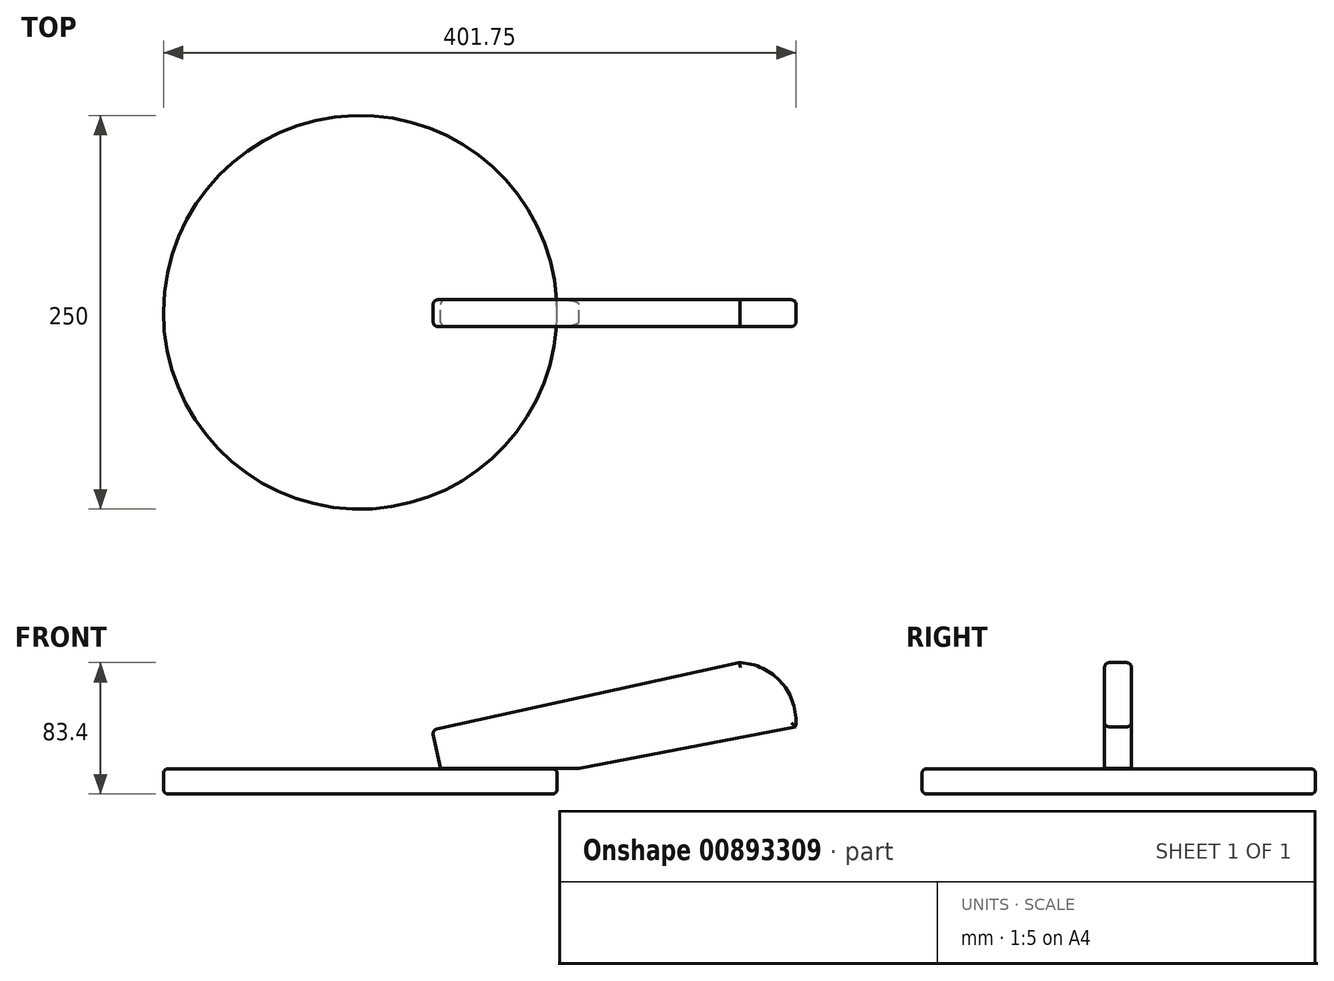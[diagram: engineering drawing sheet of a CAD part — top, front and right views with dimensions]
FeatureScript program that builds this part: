
annotation { "Feature Type Name" : "Feature", "Feature Type Description" : "" }
export const myFeature = defineFeature(function(context is Context, id is Id, definition is map)
    precondition{}
    {
        {
            var Q0;
            Q0=qCreatedBy(makeId("Top.planeOp"),FACE);
            var sketch = newSketch(context, id + "F0", { "sketchPlane" : qUnion([Q0])});
            skCircle(sketch, "E0", {"center": v(0, 0) * mm, "radius": 125 * mm});
            skSolve(sketch);
        }
        {
            var Q0;
            Q0 = qSketchRegion(id + "F0", true);
            extrude(context, id + "F1", {"entities" : qUnion([Q0]), "depth" : 16 * mm, "offsetDistance" : 25 * mm});
        }
        {
            var Q0;
            Q0=qCreatedBy(makeId("Front.planeOp"),FACE);
            var sketch = newSketch(context, id + "F2", { "sketchPlane" : qUnion([Q0])});
            skLineSegment(sketch, "E1", {"start": v(-19, 40.24) * mm, "end": v(69, 40.24) * mm});
            skLineSegment(sketch, "E2", {"start": v(69, 40.24) * mm, "end": v(206.48, 66.66) * mm});
            skLineSegment(sketch, "E3", {"start": v(-19, 40.24) * mm, "end": v(-24.35, 64.66) * mm});
            skLineSegment(sketch, "E4", {"start": v(-24.35, 64.66) * mm, "end": v(171.03, 107.4) * mm});
            skArc(sketch, "E5", {"start": v(206.48, 66.66) * mm, "mid": v(197.5, 94.64) * mm, "end": v(171.03, 107.4) * mm});
            skSolve(sketch);
        }
        {
            var Q0;
            Q0=makeQuery(id+"F2.imprint","IMPRINT",FACE,{"disambiguationData":[TD([[makeQuery(id+"F2.imprint","IMPRINT",EDGE,{"derivedFrom":sQuery(id+"F2.wireOp",EDGE,"E1")}),1.0]])]});
            extrude(context, id + "F3", {"entities" : qUnion([Q0]), "depth" : 17 * mm, "offsetDistance" : 25 * mm});
        }
        {
            var Q0;
            Q0=makeQuery(id+"F1.opExtrude","CAP_EDGE",EDGE,{"disambiguationData":[OSD([sQuery(id+"F0.wireOp",EDGE,"E0")])],"isStart":false});
            var Q1;
            Q1=makeQuery(id+"F1.opExtrude","CAP_EDGE",EDGE,{"disambiguationData":[OSD([sQuery(id+"F0.wireOp",EDGE,"E0")])],"isStart":true});
            var Q2;
            Q2=makeQuery(id+"F3.opExtrude","CAP_EDGE",EDGE,{"disambiguationData":[OSD([sQuery(id+"F2.wireOp",EDGE,"E4")])],"isStart":false});
            var Q3;
            Q3=makeQuery(id+"F3.opExtrude","CAP_EDGE",EDGE,{"disambiguationData":[OSD([sQuery(id+"F2.wireOp",EDGE,"E5")])],"isStart":false});
            var Q4;
            Q4=makeQuery(id+"F3.opExtrude","CAP_EDGE",EDGE,{"disambiguationData":[OSD([sQuery(id+"F2.wireOp",EDGE,"E5")])],"isStart":true});
            var Q5;
            Q5=makeQuery(id+"F3.opExtrude","CAP_EDGE",EDGE,{"disambiguationData":[OSD([sQuery(id+"F2.wireOp",EDGE,"E4")])],"isStart":true});
            var Q6;
            Q6=makeQuery(id+"F3.opExtrude","CAP_EDGE",EDGE,{"disambiguationData":[OSD([sQuery(id+"F2.wireOp",EDGE,"E2")])],"isStart":true});
            var Q7;
            Q7=makeQuery(id+"F3.opExtrude","CAP_EDGE",EDGE,{"disambiguationData":[OSD([sQuery(id+"F2.wireOp",EDGE,"E2")])],"isStart":false});
            var Q8;
            Q8=makeQuery(id+"F3.opExtrude","CAP_EDGE",EDGE,{"disambiguationData":[OSD([sQuery(id+"F2.wireOp",EDGE,"E3")])],"isStart":false});
            var Q9;
            Q9=makeQuery(id+"F3.opExtrude","CAP_EDGE",EDGE,{"disambiguationData":[OSD([sQuery(id+"F2.wireOp",EDGE,"E3")])],"isStart":true});
            var Q10;
            Q10=makeQuery(id+"F3.opExtrude","SWEPT_EDGE",EDGE,{"disambiguationData":[OSD([sQuery(id+"F2.wireOp",EDGE,"E3"),sQuery(id+"F2.wireOp",EDGE,"E4")])]});
            fillet(context, id + "F4", {"entities" : qUnion([Q0, Q1, Q2, Q3, Q4, Q5, Q6, Q7, Q8, Q9, Q10]), "radius" : 3 * mm, "tangentPropagation" : true, "allowEdgeOverflow" : false});
        }
        {
            var Q0;
            Q0=makeQuery(id+"F3.opExtrude","SWEPT_BODY",BODY,{"disambiguationData":[OSD([sQuery(id+"F2.wireOp",EDGE,"E1"),sQuery(id+"F2.wireOp",EDGE,"E2"),sQuery(id+"F2.wireOp",EDGE,"E3"),sQuery(id+"F2.wireOp",EDGE,"E4"),sQuery(id+"F2.wireOp",EDGE,"E5")])]});
            transform(context, id + "F5", {"entities" : qUnion([Q0]), "transformType" : TransformType.TRANSLATION_3D, "dx" : 70.1 * mm, "dy" : 8 * mm, "dz" : -24 * mm, "makeCopy" : false});
        }
    });
